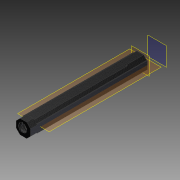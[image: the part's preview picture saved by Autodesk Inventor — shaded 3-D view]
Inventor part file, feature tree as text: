
AUTODESK INVENTOR PART (.ipt)
format: ipt  version: 2012 (Build 160160000, 160)  size: 2,033,152 bytes
history: native  units: in
note: dims shown in document units (in); Inventor stores cm internally (conversion verified against a paired STEP export)
features: reference x10, sketch x8, extrude x7, plane x3, projected_geometry x2, helix x1, fillet x1
ambient origin geometry x8: Origin, YZ Plane, XZ Plane, XY Plane, X Axis, Y Axis, Z Axis, Center Point
feature tree (32):
  plane  "Work Plane1"
  plane  "Work Plane2"
  extrude  "Extrusion7"  Depth=6.8898in TaperAngle=0.0deg
  sketch  "Sketch12"  dims[d48=1.0in d49=5.0in d50=0.0in d53=0.3937in d118=0.7559in]
  extrude  "Extrusion9"  Depth=0.3937in
  plane  "Work Plane3"
  sketch  "Sketch17"  dims[d138=0.2362in d139=0.3937in d140=12.5984in d141=0.0in d142=90.0deg d143=90.0deg d144=0.0in d145=0.0in d152=0.0118in]
  helix  "Coil8"  [1 undecoded]
  extrude  "Extrusion12"  Depth=0.1417in
  fillet  "Fillet10"  Radius=0.0906in
  extrude  "Extrusion15"  Depth=0.0118in
  extrude  "Extrusion16"  Depth=0.0118in
  extrude  "Extrusion17"  Depth=0.0118in
  extrude  "Extrusion18"  Depth=0.0118in
  sketch  "Sketch11"  dims[d0=0.04in d40=6.8898in d41=0.0in]
  reference  "Reference35"
  reference  "Reference36"
  reference  "Reference37"
  reference  "Reference38"
  sketch  "Sketch13"  dims[d119=0.7559in d122=0.1417in d131=0.0906in]
  reference  "Reference43"
  sketch  "Sketch20"  dims[d153=0.0118in d154=0.0118in]
  reference  "Reference44"
  sketch  "Sketch23"  dims[d155=0.0118in d156=0.0118in]
  reference  "Reference46"
  sketch  "Sketch24"  dims[d157=0.0118in d158=0.0118in]
  reference  "Reference47"
  reference  "Reference48"
  reference  "Reference49"
  sketch  "Sketch25"  dims[d159=0.0118in d163=0.0394in d164=0.0023in d165=0.0118in d166=0.0in d171=0.0394in d176=0.0118in d177=0.0118in d178=0.0in d179=0.0157in d180=0.0157in d181=0.3937in d182=0.0in d183=1.0in d184=0.0in d185=0.3937in d186=0.0in d188=0.0118in]
  projected_geometry  "Projected Loop6"
  projected_geometry  "Projected Loop7"
note: 1 required parameter value undecoded (feature->parameter linkage not recoverable at this tier; creation-order binding heuristic only, values carry confidence <= 0.55)
